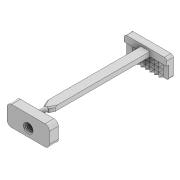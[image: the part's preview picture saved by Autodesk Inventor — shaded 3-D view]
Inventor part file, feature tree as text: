
AUTODESK INVENTOR PART (.ipt)
format: ipt  version: 2021 (Build 250183000, 183)  size: 255,488 bytes
history: native  units: mm
features: thread x1
ambient origin geometry x8: Origin, YZ Plane, XZ Plane, XY Plane, X Axis, Y Axis, Z Axis, Center Point
bodies: Solid1 (feature_tree)
feature tree (1):
  thread  "Gewinde1"  [1 undecoded]
note: 1 required parameter value undecoded (feature->parameter linkage not recoverable at this tier; creation-order binding heuristic only, values carry confidence <= 0.55)
